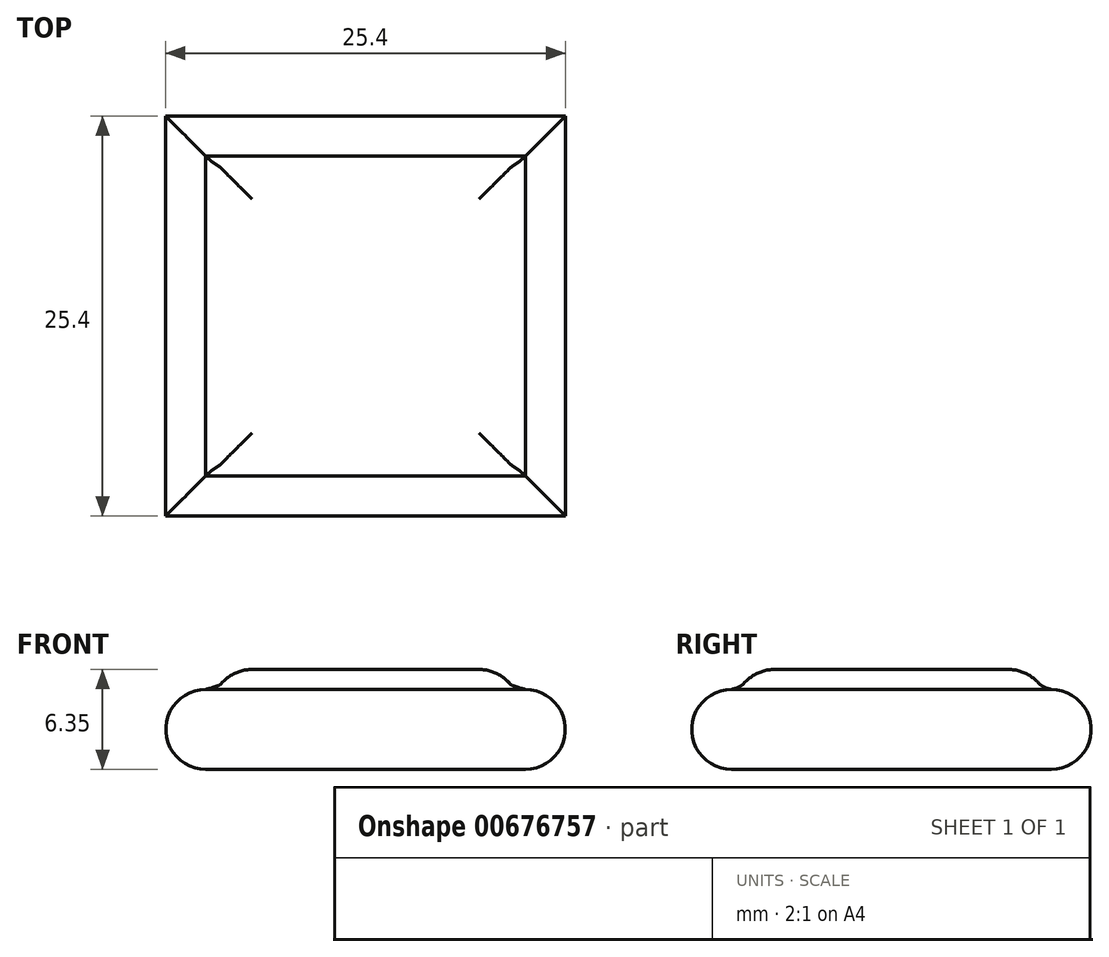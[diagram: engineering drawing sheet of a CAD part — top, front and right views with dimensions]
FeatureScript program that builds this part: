
annotation { "Feature Type Name" : "Feature", "Feature Type Description" : "" }
export const myFeature = defineFeature(function(context is Context, id is Id, definition is map)
    precondition{}
    {
        {
            var Q0;
            Q0=qCreatedBy(makeId("Front.planeOp"),FACE);
            var sketch = newSketch(context, id + "F0", { "sketchPlane" : qUnion([Q0])});
            skLineSegment(sketch, "E0", {"start": v(0, 0) * mm, "end": v(-10.16, 0) * mm});
            skLineSegment(sketch, "E1", {"start": v(-10.16, 0) * mm, "end": v(-10.16, 5.08) * mm, "construction": true});
            skLineSegment(sketch, "E2", {"start": v(10.16, 5.08) * mm, "end": v(10.16, 0) * mm, "construction": true});
            skLineSegment(sketch, "E3", {"start": v(10.16, 0) * mm, "end": v(0, 0) * mm});
            skLineSegment(sketch, "E4", {"start": v(-10.16, 5.08) * mm, "end": v(-9.2, 5.08) * mm, "construction": true});
            skLineSegment(sketch, "E5", {"start": v(-9.2, 5.08) * mm, "end": v(-8.9, 5.08) * mm, "construction": true});
            skLineSegment(sketch, "E6", {"start": v(-9.2, 5.08) * mm, "end": v(-9.2, 5.71) * mm, "construction": true});
            skLineSegment(sketch, "E7", {"start": v(-8.9, 5.08) * mm, "end": v(-8.9, 6.35) * mm, "construction": true});
            skLineSegment(sketch, "E8", {"start": v(10.16, 5.08) * mm, "end": v(9.2, 5.08) * mm, "construction": true});
            skLineSegment(sketch, "E9", {"start": v(9.2, 5.08) * mm, "end": v(8.89, 5.08) * mm, "construction": true});
            skLineSegment(sketch, "E10", {"start": v(8.89, 5.08) * mm, "end": v(8.89, 6.35) * mm, "construction": true});
            skLineSegment(sketch, "E11", {"start": v(9.2, 5.08) * mm, "end": v(9.2, 5.72) * mm, "construction": true});
            skFitSpline(sketch, "E12", {"points": [v(-10.16, 5.08) * mm, v(-9.2, 5.71) * mm, v(-8.9, 6.35) * mm], "startDerivative": vector(7.31, 1.8) * mm, "endDerivative": vector(2.53, 3.38) * mm});
            skFitSpline(sketch, "E13", {"points": [v(8.89, 6.35) * mm, v(9.2, 5.72) * mm, v(10.16, 5.08) * mm], "startDerivative": vector(2.53, -3.38) * mm, "endDerivative": vector(7.31, -1.8) * mm});
            skLineSegment(sketch, "E14", {"start": v(-7.22, 6.35) * mm, "end": v(7.22, 6.35) * mm});
            skArc(sketch, "E15.filletArc", {"start": v(9.14, 5.47) * mm, "mid": v(8.27, 6.12) * mm, "end": v(7.22, 6.35) * mm});
            skArc(sketch, "E16.filletArc", {"start": v(-7.22, 6.35) * mm, "mid": v(-8.27, 6.12) * mm, "end": v(-9.14, 5.47) * mm});
            skArc(sketch, "E17", {"start": v(10.16, 0) * mm, "mid": v(12.7, 2.54) * mm, "end": v(10.16, 5.08) * mm});
            skArc(sketch, "E18", {"start": v(-10.16, 5.08) * mm, "mid": v(-12.7, 2.54) * mm, "end": v(-10.16, 0) * mm});
            skLineSegment(sketch, "E19", {"start": v(0, 0) * mm, "end": v(0, 6.35) * mm, "construction": true});
            skLineSegment(sketch, "E20", {"start": v(10.16, 2.54) * mm, "end": v(12.7, 2.54) * mm, "construction": true});
            skSolve(sketch);
        }
        {
            var Q0;
            Q0=qSketchRegion(id+"F0",true);
            extrude(context, id + "F1", {"entities" : qUnion([Q0]), "endBound" : BoundingType.SYMMETRIC, "depth" : 25.4 * mm, "offsetDistance" : 25.4 * mm});
        }
        {
            var Q0;
            Q0=qCreatedBy(makeId("Right.planeOp"),FACE);
            var sketch = newSketch(context, id + "F2", { "sketchPlane" : qUnion([Q0])});
            skLineSegment(sketch, "E21", {"start": v(0, 0) * mm, "end": v(-10.16, 0) * mm, "construction": true});
            skLineSegment(sketch, "E22", {"start": v(0, 0) * mm, "end": v(10.16, 0) * mm, "construction": true});
            skLineSegment(sketch, "E23", {"start": v(-10.16, 0) * mm, "end": v(-10.16, 5.08) * mm, "construction": true});
            skLineSegment(sketch, "E24", {"start": v(10.16, 0) * mm, "end": v(10.16, 5.08) * mm, "construction": true});
            skLineSegment(sketch, "E25", {"start": v(-10.16, 5.08) * mm, "end": v(-9.2, 5.08) * mm, "construction": true});
            skLineSegment(sketch, "E26", {"start": v(-9.2, 5.08) * mm, "end": v(-8.9, 5.08) * mm, "construction": true});
            skLineSegment(sketch, "E27", {"start": v(-9.2, 5.08) * mm, "end": v(-9.2, 5.72) * mm, "construction": true});
            skLineSegment(sketch, "E28", {"start": v(10.16, 5.08) * mm, "end": v(9.2, 5.08) * mm, "construction": true});
            skLineSegment(sketch, "E29", {"start": v(9.2, 5.08) * mm, "end": v(8.9, 5.08) * mm, "construction": true});
            skLineSegment(sketch, "E30", {"start": v(9.2, 5.08) * mm, "end": v(9.2, 5.72) * mm, "construction": true});
            skLineSegment(sketch, "E31", {"start": v(7.44, 6.35) * mm, "end": v(-7.44, 6.35) * mm, "construction": true});
            skFitSpline(sketch, "E32", {"points": [v(-10.16, 5.08) * mm, v(-9.2, 5.72) * mm, v(-8.9, 6.35) * mm], "startDerivative": vector(3.66, 0.9) * mm, "endDerivative": vector(1.27, 1.69) * mm});
            skFitSpline(sketch, "E33", {"points": [v(8.9, 6.35) * mm, v(9.2, 5.72) * mm, v(10.16, 5.08) * mm], "startDerivative": vector(1.27, -1.69) * mm, "endDerivative": vector(3.66, -0.9) * mm});
            skArc(sketch, "E34", {"start": v(10.16, 0) * mm, "mid": v(12.7, 2.54) * mm, "end": v(10.16, 5.08) * mm});
            skArc(sketch, "E35", {"start": v(-10.16, 5.08) * mm, "mid": v(-12.7, 2.54) * mm, "end": v(-10.16, 0) * mm});
            skArc(sketch, "E36.filletArc", {"start": v(-7.44, 6.35) * mm, "mid": v(-8.49, 6.12) * mm, "end": v(-9.35, 5.48) * mm});
            skLineSegment(sketch, "E37", {"start": v(-7.44, 6.35) * mm, "end": v(-20.14, 6.35) * mm});
            skLineSegment(sketch, "E38", {"start": v(-8.9, 5.08) * mm, "end": v(-8.9, 6.35) * mm, "construction": true});
            skArc(sketch, "E39.filletArc", {"start": v(9.35, 5.48) * mm, "mid": v(8.49, 6.12) * mm, "end": v(7.44, 6.35) * mm});
            skLineSegment(sketch, "E40", {"start": v(8.9, 5.08) * mm, "end": v(8.9, 6.35) * mm, "construction": true});
            skLineSegment(sketch, "E41", {"start": v(20.14, 6.35) * mm, "end": v(7.44, 6.35) * mm});
            skLineSegment(sketch, "E42", {"start": v(0, 0) * mm, "end": v(0, 6.35) * mm, "construction": true});
            skLineSegment(sketch, "E43", {"start": v(20.14, 6.35) * mm, "end": v(20.14, 0) * mm});
            skLineSegment(sketch, "E44", {"start": v(-20.14, 6.35) * mm, "end": v(-20.14, 0) * mm});
            skLineSegment(sketch, "E45", {"start": v(-10.16, 0) * mm, "end": v(-20.14, 0) * mm});
            skLineSegment(sketch, "E46", {"start": v(-10.16, 2.54) * mm, "end": v(-12.7, 2.54) * mm, "construction": true});
            skLineSegment(sketch, "E47", {"start": v(20.14, 0) * mm, "end": v(10.16, 0) * mm});
            skSolve(sketch);
        }
        {
            var Q0;
            Q0=qSketchRegion(id+"F2",true);
            extrude(context, id + "F3", {"entities" : qUnion([Q0]), "operationType" : NewBodyOperationType.REMOVE, "endBound" : BoundingType.SYMMETRIC, "depth" : 25.4 * mm, "offsetDistance" : 25.4 * mm});
        }
    });
